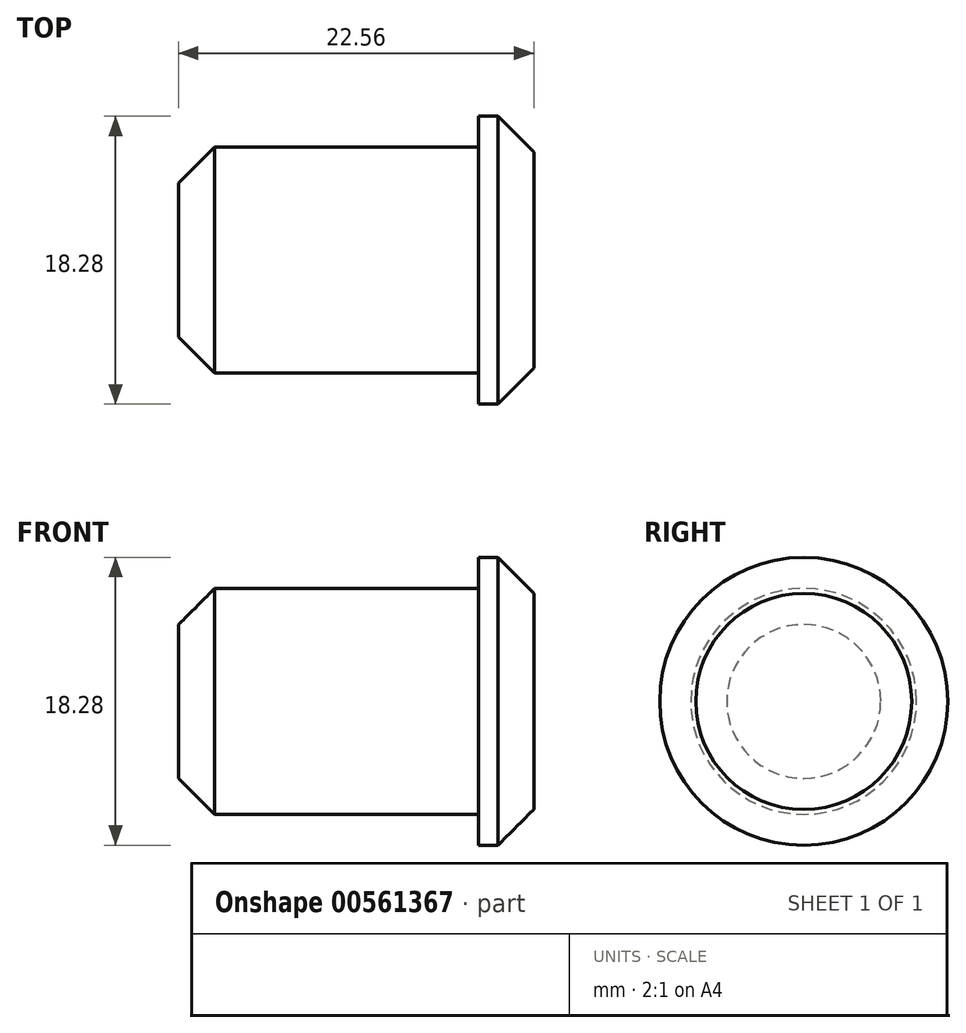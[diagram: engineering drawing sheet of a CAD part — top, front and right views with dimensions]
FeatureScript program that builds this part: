
annotation { "Feature Type Name" : "Feature", "Feature Type Description" : "" }
export const myFeature = defineFeature(function(context is Context, id is Id, definition is map)
    precondition{}
    {
        {
            var Q0;
            Q0=qCreatedBy(makeId("Top.planeOp"),FACE);
            var sketch = newSketch(context, id + "F0", { "sketchPlane" : qUnion([Q0])});
            skLineSegment(sketch, "E0.bottom", {"start": v(9.53, -7.18) * mm, "end": v(-9.53, -7.18) * mm});
            skLineSegment(sketch, "E0.top", {"start": v(9.52, 7.18) * mm, "end": v(-9.52, 7.18) * mm});
            skLineSegment(sketch, "E0.left", {"start": v(9.53, -7.18) * mm, "end": v(9.53, 7.18) * mm});
            skLineSegment(sketch, "E0.right", {"start": v(-9.53, -7.18) * mm, "end": v(-9.53, 7.18) * mm});
            skPoint(sketch, "E0.middle", {"position": v(0, 0) * mm});
            skPoint(sketch, "E1.endSnap0", {"position": v(9.53, 0) * mm});
            skLineSegment(sketch, "E2", {"start": v(9.52, 7.18) * mm, "end": v(9.52, 9.14) * mm});
            skLineSegment(sketch, "E3", {"start": v(9.52, 9.14) * mm, "end": v(13.03, 9.14) * mm});
            skLineSegment(sketch, "E4", {"start": v(13.03, 9.14) * mm, "end": v(13.03, -9.16) * mm});
            skLineSegment(sketch, "E5", {"start": v(13.03, -9.16) * mm, "end": v(9.53, -9.16) * mm});
            skLineSegment(sketch, "E6", {"start": v(9.53, -9.16) * mm, "end": v(9.53, -7.18) * mm});
            skLineSegment(sketch, "E7", {"start": v(-15.15, 0) * mm, "end": v(27.95, 0) * mm});
            skSolve(sketch);
        }
        {
            var Q0;
            {var subQ0=sQuery(id+"F0.wireOp",EDGE,"E0.top");Q0=makeQuery(id+"F0.imprint","IMPRINT",FACE,{"disambiguationData":[TD([[makeQuery(id+"F0.imprint","IMPRINT",EDGE,{"derivedFrom":subQ0}),1.0]])]});}
            var Q1;
            {var subQ1=sQuery(id+"F0.wireOp",EDGE,"E2");Q1=makeQuery(id+"F0.imprint","IMPRINT",FACE,{"disambiguationData":[TD([[makeQuery(id+"F0.imprint","IMPRINT",EDGE,{"derivedFrom":subQ1}),-1.0]])]});}
            var Q2;
            Q2=sQuery(id+"F0.wireOp",EDGE,"E7");
            revolve(context, id + "F1", {"entities" : qUnion([Q0, Q1]), "axis" : qUnion([Q2]), "revolveType" : RevolveType.FULL});
        }
        {
            var Q0;
            Q0=makeQuery(id+"F1.opRevolve","SWEPT_EDGE",EDGE,{"disambiguationData":[OSD([sQuery(id+"F0.wireOp",EDGE,"E3"),sQuery(id+"F0.wireOp",EDGE,"E4")])]});
            var Q1;
            Q1=makeQuery(id+"F1.opRevolve","SWEPT_EDGE",EDGE,{"disambiguationData":[OSD([sQuery(id+"F0.wireOp",EDGE,"E0.top"),sQuery(id+"F0.wireOp",EDGE,"E0.right")])]});
            chamfer(context, id + "F2", {"entities" : qUnion([Q0, Q1]), "width" : 2.3 * mm, "tangentPropagation" : true});
        }
    });
